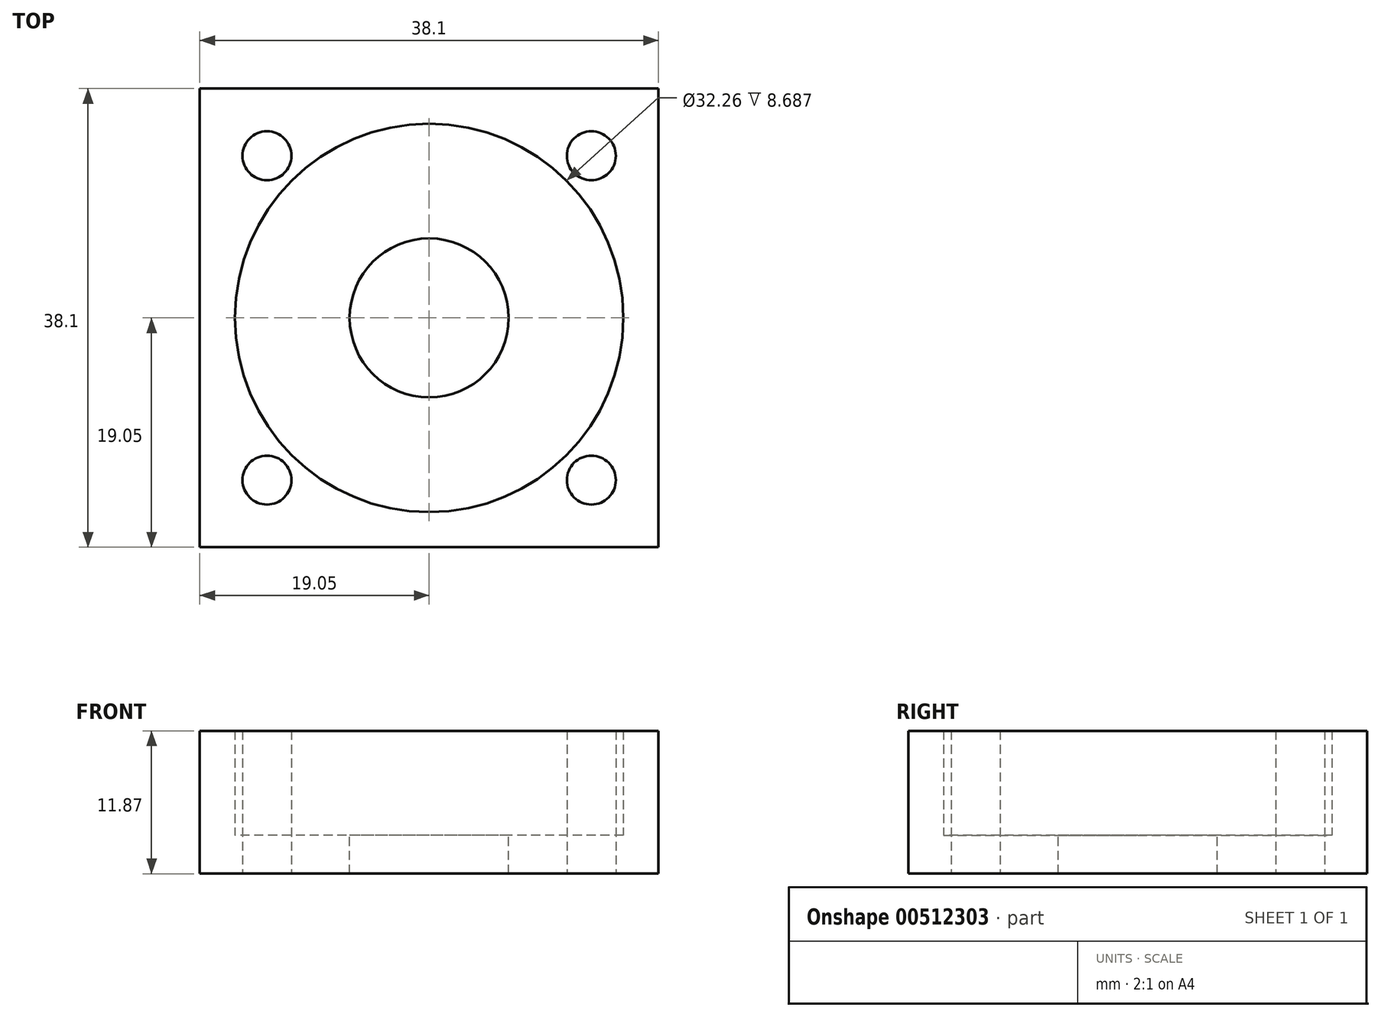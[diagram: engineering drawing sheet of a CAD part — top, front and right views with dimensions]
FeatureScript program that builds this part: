
annotation { "Feature Type Name" : "Feature", "Feature Type Description" : "" }
export const myFeature = defineFeature(function(context is Context, id is Id, definition is map)
    precondition{}
    {
        {
            var Q0;
            Q0=qCreatedBy(makeId("Top.planeOp"),FACE);
            var sketch = newSketch(context, id + "F0", { "sketchPlane" : qUnion([Q0])});
            skLineSegment(sketch, "E0.bottom", {"start": v(19.05, 19.05) * mm, "end": v(-19.05, 19.05) * mm});
            skLineSegment(sketch, "E0.top", {"start": v(19.05, -19.05) * mm, "end": v(-19.05, -19.05) * mm});
            skLineSegment(sketch, "E0.left", {"start": v(19.05, 19.05) * mm, "end": v(19.05, -19.05) * mm});
            skLineSegment(sketch, "E0.right", {"start": v(-19.05, 19.05) * mm, "end": v(-19.05, -19.05) * mm});
            skPoint(sketch, "E0.middle", {"position": v(0, 0) * mm});
            skCircle(sketch, "E1", {"center": v(0, 0) * mm, "radius": 16.13 * mm});
            skCircle(sketch, "E2", {"center": v(-13.47, -13.47) * mm, "radius": 2.03 * mm});
            skCircle(sketch, "E3", {"center": v(-13.47, 13.47) * mm, "radius": 2.03 * mm});
            skCircle(sketch, "E4", {"center": v(13.47, 13.47) * mm, "radius": 2.03 * mm});
            skCircle(sketch, "E5", {"center": v(13.47, -13.47) * mm, "radius": 2.03 * mm});
            skSolve(sketch);
        }
        {
            var Q0;
            Q0=makeQuery(id+"F0.imprint","IMPRINT",FACE,{"disambiguationData":[TD([[makeQuery(id+"F0.imprint","IMPRINT",EDGE,{"derivedFrom":sQuery(id+"F0.wireOp",EDGE,"E0.bottom")}),1.0]])]});
            extrude(context, id + "F1", {"entities" : qUnion([Q0]), "depth" : 8.7 * mm});
        }
        {
            var Q0;
            Q0=qCreatedBy(makeId("Top.planeOp"),FACE);
            var sketch = newSketch(context, id + "F2", { "sketchPlane" : qUnion([Q0])});
            skLineSegment(sketch, "E6.bottom", {"start": v(-19.05, -19.05) * mm, "end": v(19.05, -19.05) * mm});
            skLineSegment(sketch, "E6.top", {"start": v(-19.05, 19.05) * mm, "end": v(19.05, 19.05) * mm});
            skLineSegment(sketch, "E6.left", {"start": v(-19.05, -19.05) * mm, "end": v(-19.05, 19.05) * mm});
            skLineSegment(sketch, "E6.right", {"start": v(19.05, -19.05) * mm, "end": v(19.05, 19.05) * mm});
            skPoint(sketch, "E6.middle", {"position": v(0, 0) * mm});
            skCircle(sketch, "E7", {"center": v(0, 0) * mm, "radius": 6.6 * mm});
            skSolve(sketch);
        }
        {
            var Q0;
            Q0=makeQuery(id+"F2.imprint","IMPRINT",FACE,{"disambiguationData":[TD([[makeQuery(id+"F2.imprint","IMPRINT",EDGE,{"derivedFrom":sQuery(id+"F2.wireOp",EDGE,"E6.bottom")}),1.0]])]});
            extrude(context, id + "F3", {"entities" : qUnion([Q0]), "operationType" : NewBodyOperationType.ADD, "oppositeDirection" : true, "depth" : 3.17 * mm});
        }
        {
            var Q0;
            Q0=makeQuery(id+"F3.boolean.opBoolean","SPLIT",FACE,{"disambiguationData":[TD([makeQuery(id+"F1.opExtrude","SWEPT_FACE",FACE,{"disambiguationData":[OSD([sQuery(id+"F0.wireOp",EDGE,"E3")])]})])],"derivedFrom":makeQuery(id+"F3.opExtrude","CAP_FACE",FACE,{"disambiguationData":[OSD([sQuery(id+"F2.wireOp",EDGE,"E6.bottom"),sQuery(id+"F2.wireOp",EDGE,"E6.top"),sQuery(id+"F2.wireOp",EDGE,"E6.left"),sQuery(id+"F2.wireOp",EDGE,"E6.right"),sQuery(id+"F2.wireOp",EDGE,"E7")])],"isStart":true})});
            var Q1;
            Q1=makeQuery(id+"F3.boolean.opBoolean","SPLIT",FACE,{"disambiguationData":[TD([makeQuery(id+"F1.opExtrude","SWEPT_FACE",FACE,{"disambiguationData":[OSD([sQuery(id+"F0.wireOp",EDGE,"E2")])]})])],"derivedFrom":makeQuery(id+"F3.opExtrude","CAP_FACE",FACE,{"disambiguationData":[OSD([sQuery(id+"F2.wireOp",EDGE,"E6.bottom"),sQuery(id+"F2.wireOp",EDGE,"E6.top"),sQuery(id+"F2.wireOp",EDGE,"E6.left"),sQuery(id+"F2.wireOp",EDGE,"E6.right"),sQuery(id+"F2.wireOp",EDGE,"E7")])],"isStart":true})});
            var Q2;
            Q2=makeQuery(id+"F3.boolean.opBoolean","SPLIT",FACE,{"disambiguationData":[TD([makeQuery(id+"F1.opExtrude","SWEPT_FACE",FACE,{"disambiguationData":[OSD([sQuery(id+"F0.wireOp",EDGE,"E5")])]})])],"derivedFrom":makeQuery(id+"F3.opExtrude","CAP_FACE",FACE,{"disambiguationData":[OSD([sQuery(id+"F2.wireOp",EDGE,"E6.bottom"),sQuery(id+"F2.wireOp",EDGE,"E6.top"),sQuery(id+"F2.wireOp",EDGE,"E6.left"),sQuery(id+"F2.wireOp",EDGE,"E6.right"),sQuery(id+"F2.wireOp",EDGE,"E7")])],"isStart":true})});
            var Q3;
            Q3=makeQuery(id+"F3.boolean.opBoolean","SPLIT",FACE,{"disambiguationData":[TD([makeQuery(id+"F1.opExtrude","SWEPT_FACE",FACE,{"disambiguationData":[OSD([sQuery(id+"F0.wireOp",EDGE,"E4")])]})])],"derivedFrom":makeQuery(id+"F3.opExtrude","CAP_FACE",FACE,{"disambiguationData":[OSD([sQuery(id+"F2.wireOp",EDGE,"E6.bottom"),sQuery(id+"F2.wireOp",EDGE,"E6.top"),sQuery(id+"F2.wireOp",EDGE,"E6.left"),sQuery(id+"F2.wireOp",EDGE,"E6.right"),sQuery(id+"F2.wireOp",EDGE,"E7")])],"isStart":true})});
            extrude(context, id + "F4", {"entities" : qUnion([Q0, Q1, Q2, Q3]), "operationType" : NewBodyOperationType.REMOVE, "endBound" : BoundingType.UP_TO_NEXT, "oppositeDirection" : true, "depth" : 25.4 * mm});
        }
        {
            var Q0;
            Q0=makeQuery(id+"F1.opExtrude","SWEPT_BODY",BODY,{"disambiguationData":[OSD([sQuery(id+"F0.wireOp",EDGE,"E0.bottom"),sQuery(id+"F0.wireOp",EDGE,"E0.top"),sQuery(id+"F0.wireOp",EDGE,"E0.left"),sQuery(id+"F0.wireOp",EDGE,"E0.right"),sQuery(id+"F0.wireOp",EDGE,"E1"),sQuery(id+"F0.wireOp",EDGE,"E2"),sQuery(id+"F0.wireOp",EDGE,"E3"),sQuery(id+"F0.wireOp",EDGE,"E4"),sQuery(id+"F0.wireOp",EDGE,"E5")])]});
            transform(context, id + "F5", {"entities" : qUnion([Q0]), "transformType" : TransformType.TRANSLATION_3D, "dx" : 0 * mm, "dy" : 0 * mm, "dz" : 0 * mm, "makeCopy" : true});
        }
        {
            var Q0;
            Q0=makeQuery(id+"F1.opExtrude","SWEPT_BODY",BODY,{"disambiguationData":[OSD([sQuery(id+"F0.wireOp",EDGE,"E0.bottom"),sQuery(id+"F0.wireOp",EDGE,"E0.top"),sQuery(id+"F0.wireOp",EDGE,"E0.left"),sQuery(id+"F0.wireOp",EDGE,"E0.right"),sQuery(id+"F0.wireOp",EDGE,"E1"),sQuery(id+"F0.wireOp",EDGE,"E2"),sQuery(id+"F0.wireOp",EDGE,"E3"),sQuery(id+"F0.wireOp",EDGE,"E4"),sQuery(id+"F0.wireOp",EDGE,"E5")])]});
            var Q1;
            Q1=makeQuery(id+"F1.opExtrude","CAP_EDGE",EDGE,{"disambiguationData":[OSD([sQuery(id+"F0.wireOp",EDGE,"E1")])],"isStart":false});
            transform(context, id + "F6", {"entities" : qUnion([Q0]), "transformType" : TransformType.ROTATION, "transformAxis" : qUnion([Q1]), "angle" : 45 * degree, "makeCopy" : false});
        }
        {
            var Q0;
            Q0=makeQuery(id+"F5.opPattern","COPY",BODY,{"derivedFrom":makeQuery(id+"F1.opExtrude","SWEPT_BODY",BODY,{"disambiguationData":[OSD([sQuery(id+"F0.wireOp",EDGE,"E0.bottom"),sQuery(id+"F0.wireOp",EDGE,"E0.top"),sQuery(id+"F0.wireOp",EDGE,"E0.left"),sQuery(id+"F0.wireOp",EDGE,"E0.right"),sQuery(id+"F0.wireOp",EDGE,"E1"),sQuery(id+"F0.wireOp",EDGE,"E2"),sQuery(id+"F0.wireOp",EDGE,"E3"),sQuery(id+"F0.wireOp",EDGE,"E4"),sQuery(id+"F0.wireOp",EDGE,"E5")])]}),"instanceName":"1"});
            deleteBodies(context, id + "F7", {"entities" : qUnion([Q0])});
        }
        {
            var Q0;
            Q0=makeQuery(id+"F1.opExtrude","SWEPT_BODY",BODY,{"disambiguationData":[OSD([sQuery(id+"F0.wireOp",EDGE,"E0.bottom"),sQuery(id+"F0.wireOp",EDGE,"E0.top"),sQuery(id+"F0.wireOp",EDGE,"E0.left"),sQuery(id+"F0.wireOp",EDGE,"E0.right"),sQuery(id+"F0.wireOp",EDGE,"E1"),sQuery(id+"F0.wireOp",EDGE,"E2"),sQuery(id+"F0.wireOp",EDGE,"E3"),sQuery(id+"F0.wireOp",EDGE,"E4"),sQuery(id+"F0.wireOp",EDGE,"E5")])]});
            var Q1;
            Q1=makeQuery(id+"F3.opExtrude","SWEPT_FACE",FACE,{"disambiguationData":[OSD([sQuery(id+"F2.wireOp",EDGE,"E7")])]});
            transform(context, id + "F8", {"entities" : qUnion([Q0]), "transformType" : TransformType.ROTATION, "transformAxis" : qUnion([Q1]), "angle" : 45 * degree, "makeCopy" : false});
        }
        {
            var Q0;
            Q0=makeQuery(id+"F1.opExtrude","SWEPT_BODY",BODY,{"disambiguationData":[OSD([sQuery(id+"F0.wireOp",EDGE,"E0.bottom"),sQuery(id+"F0.wireOp",EDGE,"E0.top"),sQuery(id+"F0.wireOp",EDGE,"E0.left"),sQuery(id+"F0.wireOp",EDGE,"E0.right"),sQuery(id+"F0.wireOp",EDGE,"E1"),sQuery(id+"F0.wireOp",EDGE,"E2"),sQuery(id+"F0.wireOp",EDGE,"E3"),sQuery(id+"F0.wireOp",EDGE,"E4"),sQuery(id+"F0.wireOp",EDGE,"E5")])]});
            transform(context, id + "F9", {"entities" : qUnion([Q0]), "transformType" : TransformType.TRANSLATION_3D, "dx" : 40.13 * mm, "dy" : 0 * mm, "dz" : 0 * mm, "makeCopy" : true});
        }
        {
            var Q0;
            Q0=makeQuery(id+"F1.opExtrude","SWEPT_BODY",BODY,{"disambiguationData":[OSD([sQuery(id+"F0.wireOp",EDGE,"E0.bottom"),sQuery(id+"F0.wireOp",EDGE,"E0.top"),sQuery(id+"F0.wireOp",EDGE,"E0.left"),sQuery(id+"F0.wireOp",EDGE,"E0.right"),sQuery(id+"F0.wireOp",EDGE,"E1"),sQuery(id+"F0.wireOp",EDGE,"E2"),sQuery(id+"F0.wireOp",EDGE,"E3"),sQuery(id+"F0.wireOp",EDGE,"E4"),sQuery(id+"F0.wireOp",EDGE,"E5")])]});
            transform(context, id + "F10", {"entities" : qUnion([Q0]), "transformType" : TransformType.TRANSLATION_3D, "dx" : -40.13 * mm, "dy" : 0 * mm, "dz" : 0 * mm, "makeCopy" : true});
        }
        {
            var Q0;
            Q0=makeQuery(id+"F10.opPattern","COPY",BODY,{"derivedFrom":makeQuery(id+"F1.opExtrude","SWEPT_BODY",BODY,{"disambiguationData":[OSD([sQuery(id+"F0.wireOp",EDGE,"E0.bottom"),sQuery(id+"F0.wireOp",EDGE,"E0.top"),sQuery(id+"F0.wireOp",EDGE,"E0.left"),sQuery(id+"F0.wireOp",EDGE,"E0.right"),sQuery(id+"F0.wireOp",EDGE,"E1"),sQuery(id+"F0.wireOp",EDGE,"E2"),sQuery(id+"F0.wireOp",EDGE,"E3"),sQuery(id+"F0.wireOp",EDGE,"E4"),sQuery(id+"F0.wireOp",EDGE,"E5")])]}),"instanceName":"1"});
            var Q1;
            Q1=makeQuery(id+"F9.opPattern","COPY",BODY,{"derivedFrom":makeQuery(id+"F1.opExtrude","SWEPT_BODY",BODY,{"disambiguationData":[OSD([sQuery(id+"F0.wireOp",EDGE,"E0.bottom"),sQuery(id+"F0.wireOp",EDGE,"E0.top"),sQuery(id+"F0.wireOp",EDGE,"E0.left"),sQuery(id+"F0.wireOp",EDGE,"E0.right"),sQuery(id+"F0.wireOp",EDGE,"E1"),sQuery(id+"F0.wireOp",EDGE,"E2"),sQuery(id+"F0.wireOp",EDGE,"E3"),sQuery(id+"F0.wireOp",EDGE,"E4"),sQuery(id+"F0.wireOp",EDGE,"E5")])]}),"instanceName":"1"});
            deleteBodies(context, id + "F11", {"entities" : qUnion([Q0, Q1])});
        }
    });
